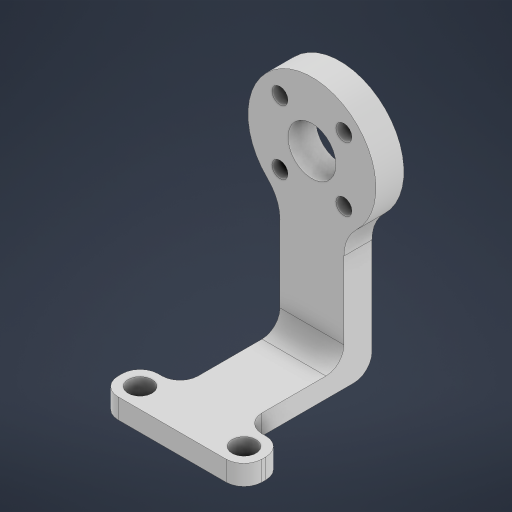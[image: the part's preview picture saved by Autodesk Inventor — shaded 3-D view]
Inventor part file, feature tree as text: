
AUTODESK INVENTOR PART (.ipt)
format: ipt  version: 2023.2 (Build 272271000, 271)  size: 274,944 bytes
history: native  units: mm
features: extrude x4, sketch x2, fillet x2, mirror x1
ambient origin geometry x8: Origin, YZ Plane, XZ Plane, XY Plane, X Axis, Y Axis, Z Axis, Center Point
bodies: Volumenkörper1 (feature_tree)
feature tree (9):
  sketch  "Skizze1"  dims[d0=25.0mm d1=25.0mm]
  extrude  "Extrusion1"  Depth=25.0mm
  extrude  "Extrusion2"  Depth=10.0mm
  extrude  "Extrusion3"  Depth=10.0mm
  extrude  "Extrusion4"  Depth=16.0mm
  mirror  "Spiegeln1"
  fillet  "Rundung1"  Radius=50.0mm
  fillet  "Rundung2"  Radius=47.5mm
  sketch  "Skizze2"  dims[d2=4.0mm d4=8.0mm d5=8.0mm d6=20.0mm d8=16.0mm d9=20.0mm d11=16.0mm d14=50.0mm d15=47.5mm d16=32.0mm d17=25.0mm d18=7.0mm d19=0.0mm d20=12.0mm d21=5.0mm d22=10.0mm d23=10.0mm d24=25.0mm d25=0.0mm d26=10.0mm d27=0.0mm d28=6.0mm d29=5.0mm d30=5.0mm d31=0.0mm d32=0.0mm d33=4.5mm d34=10.0mm]
